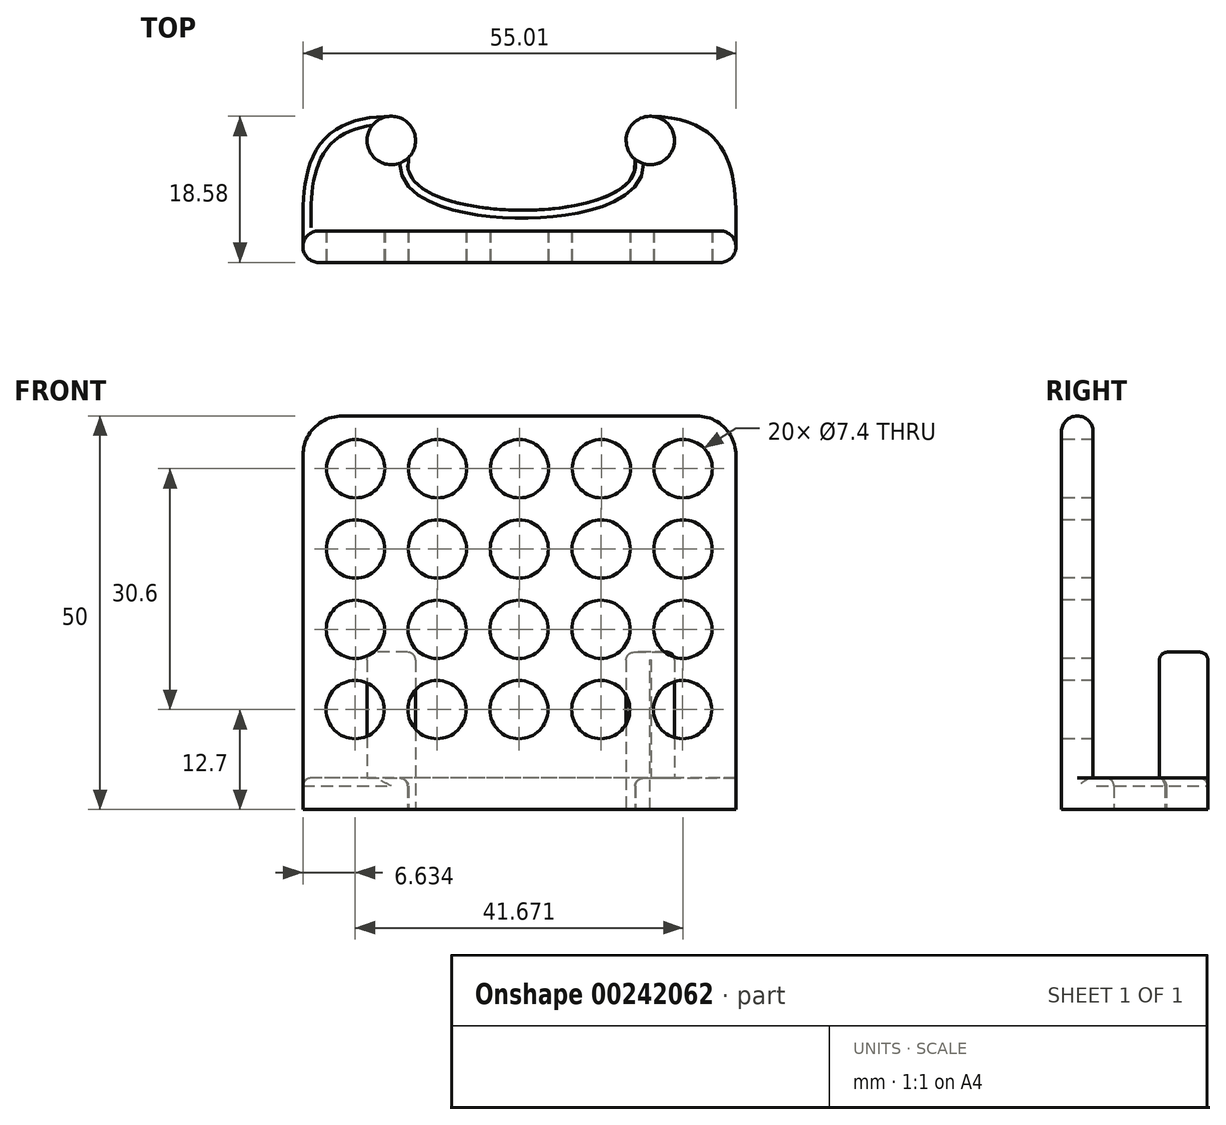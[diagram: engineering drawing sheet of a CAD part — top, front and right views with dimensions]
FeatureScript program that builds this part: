
annotation { "Feature Type Name" : "Feature", "Feature Type Description" : "" }
export const myFeature = defineFeature(function(context is Context, id is Id, definition is map)
    precondition{}
    {
        {
            var Q0;
            Q0=qCreatedBy(makeId("Top.planeOp"),FACE);
            var sketch = newSketch(context, id + "F0", { "sketchPlane" : qUnion([Q0])});
            skCircle(sketch, "E0", {"center": v(-16.45, 0) * mm, "radius": 3.08 * mm});
            skCircle(sketch, "E1", {"center": v(16.45, 0) * mm, "radius": 3.08 * mm});
            skLineSegment(sketch, "E2.bottom", {"start": v(-27.68, -11.05) * mm, "end": v(27.32, -11.05) * mm});
            skLineSegment(sketch, "E2.top", {"start": v(-27.68, -15.5) * mm, "end": v(27.32, -15.5) * mm});
            skLineSegment(sketch, "E2.left", {"start": v(-27.68, -11.05) * mm, "end": v(-27.68, -15.5) * mm});
            skLineSegment(sketch, "E2.right", {"start": v(27.32, -11.05) * mm, "end": v(27.32, -15.5) * mm});
            skFitSpline(sketch, "E3", {"points": [v(-14.28, -2.18) * mm, v(14.48, -2.37) * mm], "startDerivative": vector(-6.51, -26.62) * mm, "endDerivative": vector(-5.9, 26.05) * mm});
            skFitSpline(sketch, "E4", {"points": [v(-16.45, 3.07) * mm, v(-27.68, -11.05) * mm], "startDerivative": vector(-33.67, 0.02) * mm, "endDerivative": vector(0, -17.78) * mm});
            skFitSpline(sketch, "E5", {"points": [v(16.4, 3.07) * mm, v(27.32, -11.05) * mm], "startDerivative": vector(32.8, -0.08) * mm, "endDerivative": vector(0, -17.84) * mm});
            skLineSegment(sketch, "E6", {"start": v(27.32, -11.5) * mm, "end": v(-27.68, -11.5) * mm});
            skSolve(sketch);
        }
        {
            var Q0;
            Q0=makeQuery(id+"F0.imprint","IMPRINT",FACE,{"disambiguationData":[TD([[makeQuery(id+"F0.imprint","IMPRINT",EDGE,{"derivedFrom":sQuery(id+"F0.wireOp",EDGE,"E1")}),1.0]])]});
            var Q1;
            Q1=makeQuery(id+"F0.imprint","IMPRINT",FACE,{"disambiguationData":[TD([[makeQuery(id+"F0.imprint","IMPRINT",EDGE,{"derivedFrom":sQuery(id+"F0.wireOp",EDGE,"E0")}),1.0]])]});
            extrude(context, id + "F1", {"entities" : qUnion([Q0, Q1]), "depth" : 20 * mm});
        }
        {
            var Q0;
            {var subQ0=sQuery(id+"F0.wireOp",EDGE,"E2.top");Q0=makeQuery(id+"F0.imprint","IMPRINT",FACE,{"disambiguationData":[TD([[makeQuery(id+"F0.imprint","IMPRINT",EDGE,{"derivedFrom":subQ0}),1.0]])]});}
            extrude(context, id + "F2", {"entities" : qUnion([Q0]), "depth" : 50 * mm});
        }
        {
            var Q0;
            {var subQ1=sQuery(id+"F0.wireOp",EDGE,"E2.bottom");Q0=makeQuery(id+"F0.imprint","IMPRINT",FACE,{"disambiguationData":[TD([[makeQuery(id+"F0.imprint","IMPRINT",EDGE,{"derivedFrom":subQ1}),1.0]])]});}
            var Q1;
            {var subQ0=sQuery(id+"F0.wireOp",EDGE,"E2.bottom");Q1=makeQuery(id+"F0.imprint","IMPRINT",FACE,{"disambiguationData":[TD([[makeQuery(id+"F0.imprint","IMPRINT",EDGE,{"derivedFrom":subQ0}),-1.0]])]});}
            extrude(context, id + "F3", {"entities" : qUnion([Q0, Q1]), "depth" : 4 * mm});
        }
        {
            var Q0;
            Q0=makeQuery(id+"F2.opExtrude","SWEPT_FACE",FACE,{"disambiguationData":[OSD([sQuery(id+"F0.wireOp",EDGE,"E2.top")])]});
            var sketch = newSketch(context, id + "F4", { "sketchPlane" : qUnion([Q0])});
            skCircle(sketch, "E7", {"center": v(-20.97, 43.3) * mm, "radius": 3.7 * mm});
            skCircle(sketch, "E8.1.0.0", {"center": v(-10.57, 43.3) * mm, "radius": 3.7 * mm});
            skCircle(sketch, "E8.2.0.0", {"center": v(-0.17, 43.3) * mm, "radius": 3.7 * mm});
            skCircle(sketch, "E8.3.0.0", {"center": v(10.23, 43.3) * mm, "radius": 3.7 * mm});
            skCircle(sketch, "E8.4.0.0", {"center": v(20.63, 43.3) * mm, "radius": 3.7 * mm});
            skLineSegment(sketch, "E8.direction1", {"start": v(-20.97, 43.3) * mm, "end": v(-10.57, 43.3) * mm, "construction": true});
            skCircle(sketch, "E9.1.0.0", {"center": v(-21, 33.1) * mm, "radius": 3.7 * mm});
            skCircle(sketch, "E9.1.0.1", {"center": v(-10.6, 33.1) * mm, "radius": 3.7 * mm});
            skCircle(sketch, "E9.1.0.2", {"center": v(-0.2, 33.1) * mm, "radius": 3.7 * mm});
            skCircle(sketch, "E9.1.0.3", {"center": v(10.2, 33.1) * mm, "radius": 3.7 * mm});
            skCircle(sketch, "E9.1.0.4", {"center": v(20.6, 33.1) * mm, "radius": 3.7 * mm});
            skCircle(sketch, "E9.2.0.0", {"center": v(-21.02, 22.9) * mm, "radius": 3.7 * mm});
            skCircle(sketch, "E9.2.0.1", {"center": v(-10.62, 22.9) * mm, "radius": 3.7 * mm});
            skCircle(sketch, "E9.2.0.2", {"center": v(-0.22, 22.9) * mm, "radius": 3.7 * mm});
            skCircle(sketch, "E9.2.0.3", {"center": v(10.18, 22.9) * mm, "radius": 3.7 * mm});
            skCircle(sketch, "E9.2.0.4", {"center": v(20.58, 22.9) * mm, "radius": 3.7 * mm});
            skCircle(sketch, "E9.3.0.0", {"center": v(-21.05, 12.7) * mm, "radius": 3.7 * mm});
            skCircle(sketch, "E9.3.0.1", {"center": v(-10.65, 12.7) * mm, "radius": 3.7 * mm});
            skCircle(sketch, "E9.3.0.2", {"center": v(-0.25, 12.7) * mm, "radius": 3.7 * mm});
            skCircle(sketch, "E9.3.0.3", {"center": v(10.15, 12.7) * mm, "radius": 3.7 * mm});
            skCircle(sketch, "E9.3.0.4", {"center": v(20.55, 12.7) * mm, "radius": 3.7 * mm});
            skLineSegment(sketch, "E9.direction1", {"start": v(-20.97, 43.3) * mm, "end": v(-21, 33.1) * mm, "construction": true});
            skSolve(sketch);
        }
        {
            var Q0;
            Q0=makeQuery(id+"F4.imprint","IMPRINT",FACE,{"disambiguationData":[TD([[makeQuery(id+"F4.imprint","IMPRINT",EDGE,{"derivedFrom":sQuery(id+"F4.wireOp",EDGE,"E7")}),1.0]])]});
            var Q1;
            Q1=makeQuery(id+"F4.imprint","IMPRINT",FACE,{"disambiguationData":[TD([[makeQuery(id+"F4.imprint","IMPRINT",EDGE,{"derivedFrom":sQuery(id+"F4.wireOp",EDGE,"E9.1.0.0")}),1.0]])]});
            var Q2;
            Q2=makeQuery(id+"F4.imprint","IMPRINT",FACE,{"disambiguationData":[TD([[makeQuery(id+"F4.imprint","IMPRINT",EDGE,{"derivedFrom":sQuery(id+"F4.wireOp",EDGE,"E9.2.0.0")}),1.0]])]});
            var Q3;
            Q3=makeQuery(id+"F4.imprint","IMPRINT",FACE,{"disambiguationData":[TD([[makeQuery(id+"F4.imprint","IMPRINT",EDGE,{"derivedFrom":sQuery(id+"F4.wireOp",EDGE,"E9.3.0.0")}),1.0]])]});
            var Q4;
            Q4=makeQuery(id+"F4.imprint","IMPRINT",FACE,{"disambiguationData":[TD([[makeQuery(id+"F4.imprint","IMPRINT",EDGE,{"derivedFrom":sQuery(id+"F4.wireOp",EDGE,"E9.3.0.1")}),1.0]])]});
            var Q5;
            Q5=makeQuery(id+"F4.imprint","IMPRINT",FACE,{"disambiguationData":[TD([[makeQuery(id+"F4.imprint","IMPRINT",EDGE,{"derivedFrom":sQuery(id+"F4.wireOp",EDGE,"E9.3.0.2")}),1.0]])]});
            var Q6;
            Q6=makeQuery(id+"F4.imprint","IMPRINT",FACE,{"disambiguationData":[TD([[makeQuery(id+"F4.imprint","IMPRINT",EDGE,{"derivedFrom":sQuery(id+"F4.wireOp",EDGE,"E9.3.0.4")}),1.0]])]});
            var Q7;
            Q7=makeQuery(id+"F4.imprint","IMPRINT",FACE,{"disambiguationData":[TD([[makeQuery(id+"F4.imprint","IMPRINT",EDGE,{"derivedFrom":sQuery(id+"F4.wireOp",EDGE,"E9.3.0.3")}),1.0]])]});
            var Q8;
            Q8=makeQuery(id+"F4.imprint","IMPRINT",FACE,{"disambiguationData":[TD([[makeQuery(id+"F4.imprint","IMPRINT",EDGE,{"derivedFrom":sQuery(id+"F4.wireOp",EDGE,"E9.2.0.4")}),1.0]])]});
            var Q9;
            Q9=makeQuery(id+"F4.imprint","IMPRINT",FACE,{"disambiguationData":[TD([[makeQuery(id+"F4.imprint","IMPRINT",EDGE,{"derivedFrom":sQuery(id+"F4.wireOp",EDGE,"E9.2.0.3")}),1.0]])]});
            var Q10;
            Q10=makeQuery(id+"F4.imprint","IMPRINT",FACE,{"disambiguationData":[TD([[makeQuery(id+"F4.imprint","IMPRINT",EDGE,{"derivedFrom":sQuery(id+"F4.wireOp",EDGE,"E9.2.0.2")}),1.0]])]});
            var Q11;
            Q11=makeQuery(id+"F4.imprint","IMPRINT",FACE,{"disambiguationData":[TD([[makeQuery(id+"F4.imprint","IMPRINT",EDGE,{"derivedFrom":sQuery(id+"F4.wireOp",EDGE,"E9.2.0.1")}),1.0]])]});
            var Q12;
            Q12=makeQuery(id+"F4.imprint","IMPRINT",FACE,{"disambiguationData":[TD([[makeQuery(id+"F4.imprint","IMPRINT",EDGE,{"derivedFrom":sQuery(id+"F4.wireOp",EDGE,"E9.1.0.1")}),1.0]])]});
            var Q13;
            Q13=makeQuery(id+"F4.imprint","IMPRINT",FACE,{"disambiguationData":[TD([[makeQuery(id+"F4.imprint","IMPRINT",EDGE,{"derivedFrom":sQuery(id+"F4.wireOp",EDGE,"E9.1.0.2")}),1.0]])]});
            var Q14;
            Q14=makeQuery(id+"F4.imprint","IMPRINT",FACE,{"disambiguationData":[TD([[makeQuery(id+"F4.imprint","IMPRINT",EDGE,{"derivedFrom":sQuery(id+"F4.wireOp",EDGE,"E8.1.0.0")}),1.0]])]});
            var Q15;
            Q15=makeQuery(id+"F4.imprint","IMPRINT",FACE,{"disambiguationData":[TD([[makeQuery(id+"F4.imprint","IMPRINT",EDGE,{"derivedFrom":sQuery(id+"F4.wireOp",EDGE,"E8.2.0.0")}),1.0]])]});
            var Q16;
            Q16=makeQuery(id+"F4.imprint","IMPRINT",FACE,{"disambiguationData":[TD([[makeQuery(id+"F4.imprint","IMPRINT",EDGE,{"derivedFrom":sQuery(id+"F4.wireOp",EDGE,"E8.3.0.0")}),1.0]])]});
            var Q17;
            Q17=makeQuery(id+"F4.imprint","IMPRINT",FACE,{"disambiguationData":[TD([[makeQuery(id+"F4.imprint","IMPRINT",EDGE,{"derivedFrom":sQuery(id+"F4.wireOp",EDGE,"E9.1.0.3")}),1.0]])]});
            var Q18;
            Q18=makeQuery(id+"F4.imprint","IMPRINT",FACE,{"disambiguationData":[TD([[makeQuery(id+"F4.imprint","IMPRINT",EDGE,{"derivedFrom":sQuery(id+"F4.wireOp",EDGE,"E9.1.0.4")}),1.0]])]});
            var Q19;
            Q19=makeQuery(id+"F4.imprint","IMPRINT",FACE,{"disambiguationData":[TD([[makeQuery(id+"F4.imprint","IMPRINT",EDGE,{"derivedFrom":sQuery(id+"F4.wireOp",EDGE,"E8.4.0.0")}),1.0]])]});
            extrude(context, id + "F5", {"entities" : qUnion([Q0, Q1, Q2, Q3, Q4, Q5, Q6, Q7, Q8, Q9, Q10, Q11, Q12, Q13, Q14, Q15, Q16, Q17, Q18, Q19]), "operationType" : NewBodyOperationType.REMOVE, "oppositeDirection" : true, "depth" : 10 * mm});
        }
        {
            var Q0;
            Q0=makeQuery(id+"F2.opExtrude","CAP_EDGE",EDGE,{"disambiguationData":[OSD([sQuery(id+"F0.wireOp",EDGE,"E2.left")])],"isStart":false});
            var Q1;
            Q1=makeQuery(id+"F2.opExtrude","CAP_EDGE",EDGE,{"disambiguationData":[OSD([sQuery(id+"F0.wireOp",EDGE,"E2.right")])],"isStart":false});
            fillet(context, id + "F6", {"entities" : qUnion([Q0, Q1]), "radius" : 5 * mm, "tangentPropagation" : true, "allowEdgeOverflow" : false});
        }
        {
            var Q0;
            Q0=makeQuery(id+"F2.opExtrude","SWEPT_BODY",BODY,{"disambiguationData":[OSD([sQuery(id+"F0.wireOp",EDGE,"E2.bottom"),sQuery(id+"F0.wireOp",EDGE,"E2.top"),sQuery(id+"F0.wireOp",EDGE,"E2.left"),sQuery(id+"F0.wireOp",EDGE,"E2.right")])]});
            var Q1;
            Q1=makeQuery(id+"F3.opExtrude","SWEPT_BODY",BODY,{"disambiguationData":[OSD([sQuery(id+"F0.wireOp",EDGE,"E0"),sQuery(id+"F0.wireOp",EDGE,"E1"),sQuery(id+"F0.wireOp",EDGE,"E2.bottom"),sQuery(id+"F0.wireOp",EDGE,"E3"),sQuery(id+"F0.wireOp",EDGE,"E4"),sQuery(id+"F0.wireOp",EDGE,"ad43e9fe-9ed4-43e3-8d50-cd4760d36b880.MirrorCS")])]});
            var Q2;
            Q2=makeQuery(id+"F1.opExtrude","SWEPT_BODY",BODY,{"disambiguationData":[OSD([sQuery(id+"F0.wireOp",EDGE,"E1"),sQuery(id+"F0.wireOp",EDGE,"ad43e9fe-9ed4-43e3-8d50-cd4760d36b880.MirrorCS")])]});
            var Q3;
            Q3=makeQuery(id+"F1.opExtrude","SWEPT_BODY",BODY,{"disambiguationData":[OSD([sQuery(id+"F0.wireOp",EDGE,"E0"),sQuery(id+"F0.wireOp",EDGE,"E4")])]});
            booleanBodies(context, id + "F7", {"operationType" : BooleanOperationType.UNION, "tools" : qUnion([Q0, Q1, Q2, Q3])});
        }
        {
            var Q0;
            Q0=makeQuery(id+"F7.opBoolean","SPLIT",EDGE,{"derivedFrom":makeQuery(id+"F2.opExtrude","SWEPT_EDGE",EDGE,{"disambiguationData":[OSD([sQuery(id+"F0.wireOp",EDGE,"E2.bottom"),sQuery(id+"F0.wireOp",EDGE,"E2.left"),sQuery(id+"F0.wireOp",EDGE,"E4")])]})});
            var Q1;
            Q1=makeQuery(id+"F2.opExtrude","SWEPT_EDGE",EDGE,{"disambiguationData":[OSD([sQuery(id+"F0.wireOp",EDGE,"E2.top"),sQuery(id+"F0.wireOp",EDGE,"E2.left")])]});
            fillet(context, id + "F8", {"entities" : qUnion([Q0, Q1]), "radius" : 2 * mm, "tangentPropagation" : true, "allowEdgeOverflow" : false});
        }
        {
            var Q0;
            Q0=makeQuery(id+"F3.opExtrude","CAP_EDGE",EDGE,{"disambiguationData":[OSD([sQuery(id+"F0.wireOp",EDGE,"ad43e9fe-9ed4-43e3-8d50-cd4760d36b880.MirrorCS")])],"isStart":false});
            var Q1;
            Q1=makeQuery(id+"F3.opExtrude","CAP_EDGE",EDGE,{"disambiguationData":[OSD([sQuery(id+"F0.wireOp",EDGE,"E4")])],"isStart":false});
            var Q2;
            {var subQ0=sQuery(id+"F0.wireOp",EDGE,"E3");Q2=makeQuery(id+"F5.boolean.opBoolean","SPLIT",EDGE,{"disambiguationData":[TD([makeQuery(id+"F5.opExtrude","SWEPT_FACE",FACE,{"disambiguationData":[OSD([sQuery(id+"F4.wireOp",EDGE,"182ccb3f-6eeb-4634-bd95-0a4b658be1e7.3.0.10")])]})])],"derivedFrom":makeQuery(id+"F3.opExtrude","CAP_EDGE",EDGE,{"disambiguationData":[OSD([subQ0])],"isStart":false})});}
            var Q3;
            {var subQ0=sQuery(id+"F0.wireOp",EDGE,"E3");Q3=makeQuery(id+"F5.boolean.opBoolean","SPLIT",EDGE,{"disambiguationData":[TD([makeQuery(id+"F5.opExtrude","SWEPT_FACE",FACE,{"disambiguationData":[OSD([sQuery(id+"F4.wireOp",EDGE,"182ccb3f-6eeb-4634-bd95-0a4b658be1e7.3.0.14")])]})])],"derivedFrom":makeQuery(id+"F3.opExtrude","CAP_EDGE",EDGE,{"disambiguationData":[OSD([subQ0])],"isStart":false})});}
            var Q4;
            {var subQ0=sQuery(id+"F0.wireOp",EDGE,"E3");var subQ1=sQuery(id+"F0.wireOp",EDGE,"E1");Q4=makeQuery(id+"F5.boolean.opBoolean","SPLIT",EDGE,{"disambiguationData":[TD([makeQuery(id+"F3.opExtrude","SWEPT_FACE",FACE,{"disambiguationData":[OSD([subQ1])]})])],"derivedFrom":makeQuery(id+"F3.opExtrude","CAP_EDGE",EDGE,{"disambiguationData":[OSD([subQ0])],"isStart":false})});}
            var Q5;
            {var subQ0=sQuery(id+"F0.wireOp",EDGE,"E0");var subQ1=sQuery(id+"F0.wireOp",EDGE,"E3");Q5=makeQuery(id+"F5.boolean.opBoolean","SPLIT",EDGE,{"disambiguationData":[TD([makeQuery(id+"F3.opExtrude","SWEPT_FACE",FACE,{"disambiguationData":[OSD([subQ0])]})])],"derivedFrom":makeQuery(id+"F3.opExtrude","CAP_EDGE",EDGE,{"disambiguationData":[OSD([subQ1])],"isStart":false})});}
            var Q6;
            Q6=makeQuery(id+"F1.opExtrude","CAP_EDGE",EDGE,{"disambiguationData":[OSD([sQuery(id+"F0.wireOp",EDGE,"E0")])],"isStart":false});
            var Q7;
            Q7=makeQuery(id+"F1.opExtrude","CAP_EDGE",EDGE,{"disambiguationData":[OSD([sQuery(id+"F0.wireOp",EDGE,"E1")])],"isStart":false});
            fillet(context, id + "F9", {"entities" : qUnion([Q0, Q1, Q2, Q3, Q4, Q5, Q6, Q7]), "radius" : 1 * mm, "tangentPropagation" : true, "allowEdgeOverflow" : false});
        }
    });
